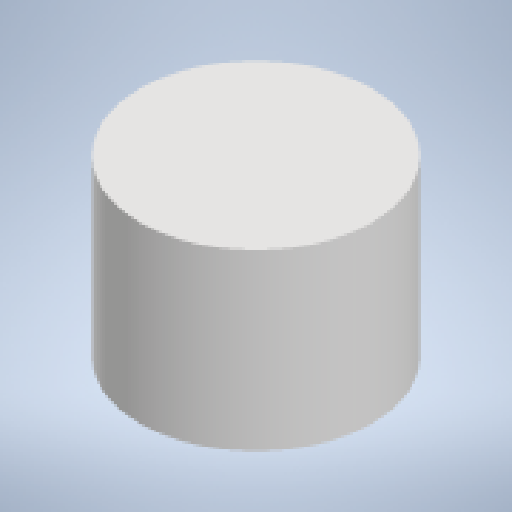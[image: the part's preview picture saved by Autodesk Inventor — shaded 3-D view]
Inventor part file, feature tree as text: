
AUTODESK INVENTOR PART (.ipt)
format: ipt  version: 2023 (Build 270158000, 158)  size: 187,904 bytes
history: native  units: mm
features: extrude x1, sketch x1
ambient origin geometry x8: Origin, YZ Plane, XZ Plane, XY Plane, X Axis, Y Axis, Z Axis, Center Point
bodies: Solid1 (feature_tree)
feature tree (2):
  extrude  "Extrusion1"  Depth=6.0mm TaperAngle=0.0deg
  sketch  "Sketch1"  dims[d0=8.0mm d1=6.0mm d2=0.0mm]
